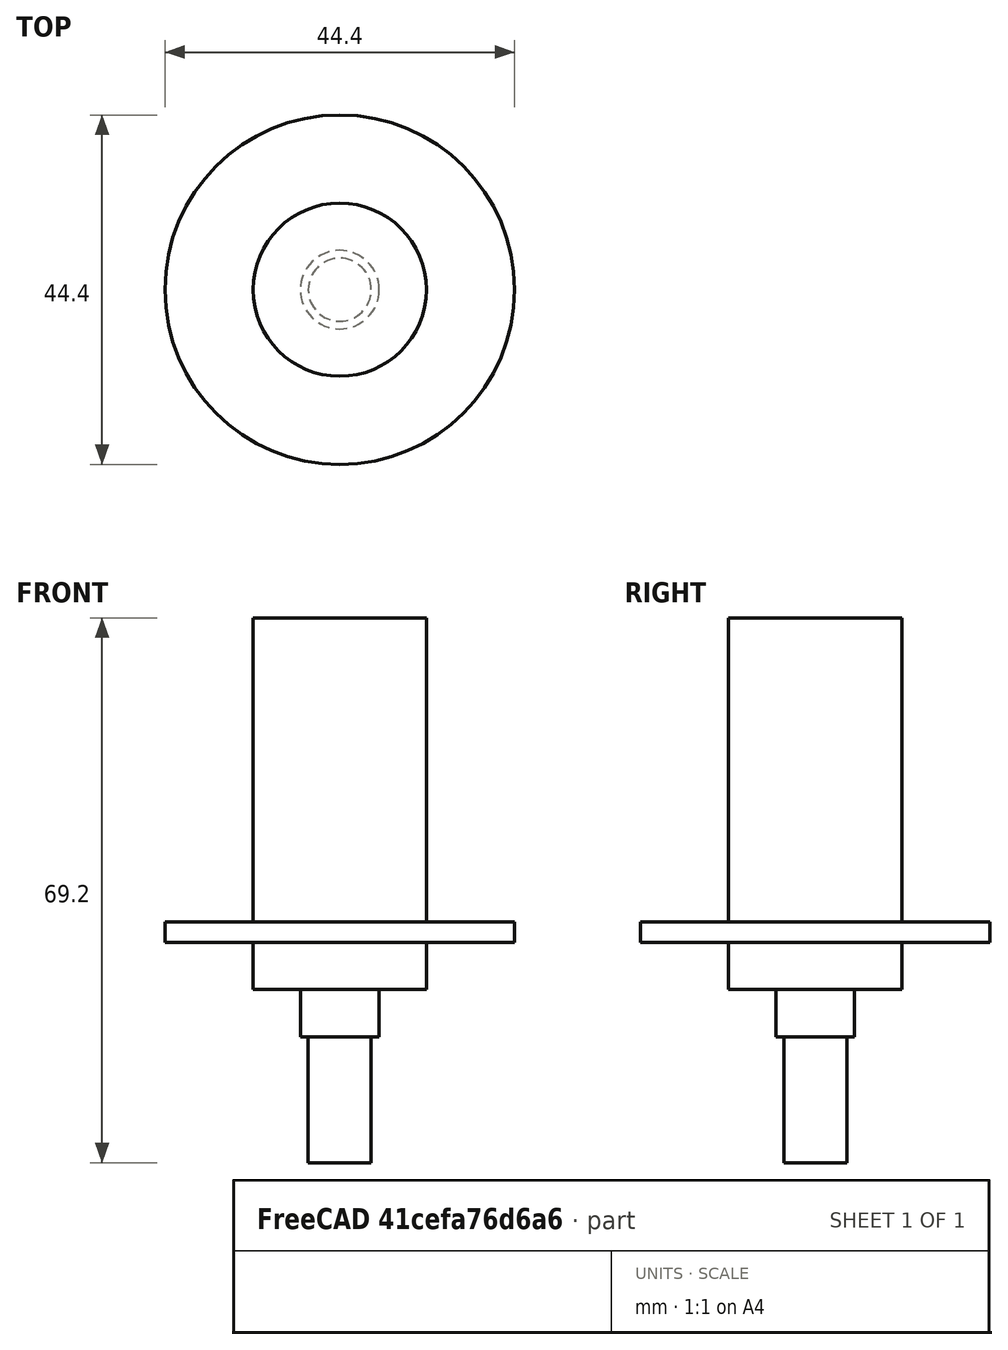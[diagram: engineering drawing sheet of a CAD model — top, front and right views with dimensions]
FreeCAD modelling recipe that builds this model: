
FCSTD DOCUMENT  (FreeCAD 0.20R29410 (Git))
Label: SlipRing
License: All rights reserved
LicenseURL: http://en.wikipedia.org/wiki/All_rights_reserved
objects: App::DocumentObjectGroup×3, PartDesign::CoordinateSystem×1, App::FeaturePython×1, Sketcher::SketchObject×1, PartDesign::Revolution×1, PartDesign::Body×1, App::Part×1
note: 5 computed .brp shape members not serialized (recipe doc carries the construction recipe); baked Part::Feature solids carry a one-line shape summary decoded from their .brp

FEATURE [App::DocumentObjectGroup] Parts
FEATURE [PartDesign::CoordinateSystem] LCS_Origin
  AttacherType = Attacher::AttachEngine3D
  MapMode = 2
  Support = -> [X_Axis]
FEATURE [App::FeaturePython] Variables  # WARN: FeaturePython — macro-defined, semantics opaque (R4)
  Type = App::PropertyContainer
FEATURE [App::DocumentObjectGroup] Constraints
FEATURE [App::DocumentObjectGroup] Configurations
FEATURE [Sketcher::SketchObject] Sketch
  FullyConstrained = true
  MapMode = 5
  Placement = pos=(0,0,0) rot=(1,0,0;1.5708rad)
  Support = -> [XZ_Plane001]
  sketch-geometry (14):
    g0: LineSegment StartX=0 StartY=38.6 StartZ=0 EndX=11 EndY=38.6 EndZ=0
    g1: LineSegment StartX=11 StartY=38.6 StartZ=0 EndX=11 EndY=0 EndZ=0
    g2: LineSegment StartX=11 StartY=0 StartZ=0 EndX=22.2 EndY=0 EndZ=0
    g3: LineSegment StartX=22.2 StartY=0 StartZ=0 EndX=22.2 EndY=-2.6 EndZ=0
    g4: LineSegment StartX=22.2 StartY=-2.6 StartZ=0 EndX=11 EndY=-2.6 EndZ=0
    g5: LineSegment StartX=11 StartY=-2.6 StartZ=0 EndX=11 EndY=-8.6 EndZ=0
    g6: LineSegment StartX=11 StartY=-8.6 StartZ=0 EndX=5 EndY=-8.6 EndZ=0
    g7: LineSegment StartX=5 StartY=-8.6 StartZ=0 EndX=5 EndY=-14.6 EndZ=0
    g8: LineSegment StartX=0 StartY=-14.6 StartZ=0 EndX=0 EndY=38.6 EndZ=0
    g9: LineSegment StartX=5 StartY=-14.6 StartZ=0 EndX=4 EndY=-14.6 EndZ=0
    g10: LineSegment StartX=4 StartY=-14.6 StartZ=0 EndX=0 EndY=-14.6 EndZ=0
    g11: LineSegment StartX=4 StartY=-14.6 StartZ=0 EndX=4 EndY=-30.6 EndZ=0
    g12: LineSegment StartX=4 StartY=-30.6 StartZ=0 EndX=0 EndY=-30.6 EndZ=0
    g13: LineSegment StartX=0 StartY=-30.6 StartZ=0 EndX=0 EndY=-14.6 EndZ=0
  constraints (41):
    c: PointOnObject(g0,g-2)
    c: Horizontal(g0)
    c: Coincident(g0,g1)
    c: Vertical(g1)
    c: Coincident(g1,g2)
    c: Horizontal(g2)
    c: Coincident(g2,g3)
    c: Vertical(g3)
    c: Coincident(g3,g4)
    c: Horizontal(g4)
    c: Coincident(g4,g5)
    c: Vertical(g5)
    c: Coincident(g5,g6)
    c: Coincident(g6,g7)
    c: Vertical(g7)
    c: Coincident(g7,g9)
    c: PointOnObject(g10,g-2)
    c: Coincident(g10,g8)
    c: Coincident(g8,g0)
    c: Horizontal(g6)
    c: DistanceX(g0,g0) = 11
    c: DistanceX(g-1,g3) = 22.2
    c: PointOnObject(g1,g5)
    c: DistanceX(g10,g9) = 5
    c: DistanceY(g7,g7) = 6
    c: DistanceY(g5,g5) = 6
    c: DistanceY(g3,g3) = 2.6
    c: DistanceY(g1,g1) = 38.6
    c: PointOnObject(g1,g-1)
    c: Coincident(g9,g10)
    c: Horizontal(g9)
    c: Horizontal(g10)
    c: Coincident(g11,g9)
    c: Vertical(g11)
    c: Coincident(g12,g11)
    c: PointOnObject(g12,g-2)
    c: Horizontal(g12)
    c: Coincident(g13,g12)
    c: Coincident(g13,g8)
    c: DistanceX(g12,g12) = 4
    c: DistanceY(g13,g13) = 16
FEATURE [PartDesign::Revolution] Revolution
  Angle = 360
  Axis = (0,-2e-16,1)
  Base = (0,0,0)
  Placement = pos=(0,0,0) rot=(1,0,0;1.5708rad)
  Profile = -> Sketch
  ReferenceAxis = -> Sketch [V_Axis]
  Reversed = true
FEATURE [PartDesign::Body] Body
  Group = -> [Sketch,Revolution]
  Origin = -> Origin001
  Tip = -> Revolution
FEATURE [App::Part] Assembly
  AssemblyType = Part::Link
  Group = -> [LCS_Origin,Variables,Constraints,Configurations,Body]
  Origin = -> Origin
  Type = Assembly
